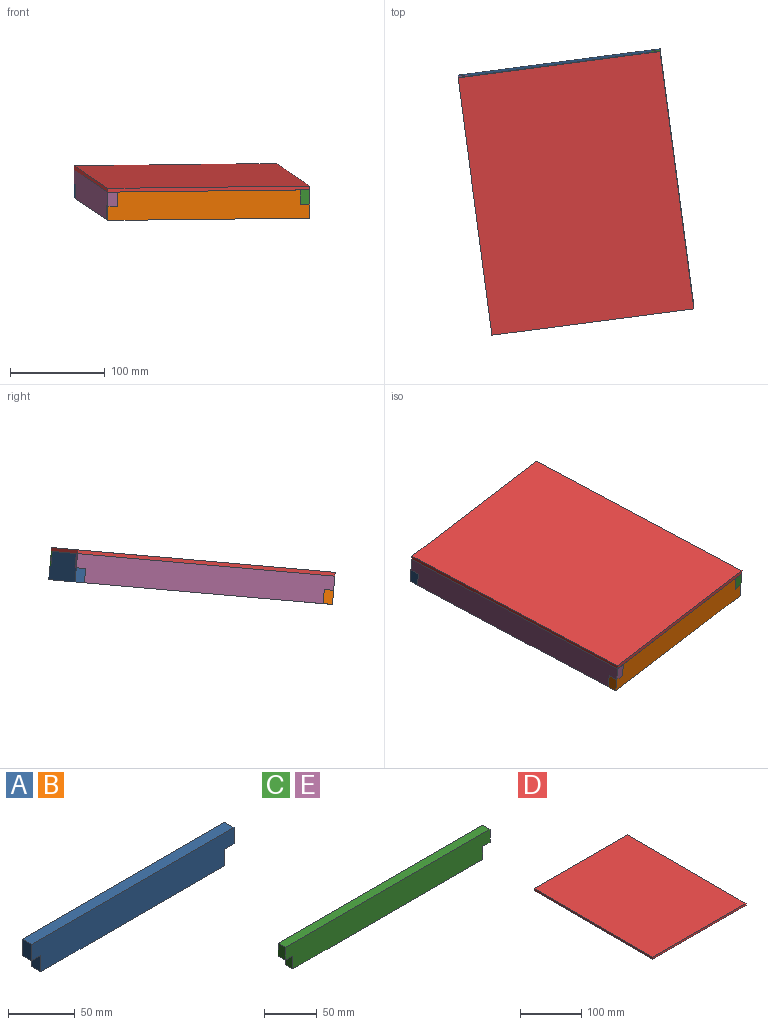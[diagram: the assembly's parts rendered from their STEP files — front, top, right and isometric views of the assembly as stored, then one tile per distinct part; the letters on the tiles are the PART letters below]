
ASSEMBLY  parts=5 mates=4
PART A: 10 faces, bbox 215x10x30 mm
  f0: plane 195x10mm, normal (0,0,-1), area 1950mm2, adj f1,f2,f7,f9
  f1: plane 215x30mm, normal (0,-1,0), area 6150mm2, adj f0,f3,f4,f5,f6,f7,f8,f9
  f2: plane 215x30mm, normal (0,1,0), area 6150mm2, adj f0,f3,f4,f5,f6,f7,f8,f9
  f3: plane 215x10mm, normal (0,0,1), area 2150mm2, adj f1,f2,f4,f5
  f4: plane 15x10mm, normal (-1,0,0), area 150mm2, adj f1,f2,f3,f6
  f5: plane 15x10mm, normal (1,0,0), area 150mm2, adj f1,f2,f3,f8
  f6: plane 10x10mm, normal (0,0,-1), area 100mm2, adj f1,f2,f4,f7
  f7: plane 15x10mm, normal (-1,0,0), area 150mm2, adj f0,f1,f2,f6
  f8: plane 10x10mm, normal (0,0,-1), area 100mm2, adj f1,f2,f5,f9
  f9: plane 15x10mm, normal (1,0,0), area 150mm2, adj f0,f1,f2,f8
PART B: same geometry as A
PART C: 10 faces, bbox 275x10x30 mm
  f0: plane 255x10mm, normal (0,0,-1), area 2550mm2, adj f1,f2,f7,f9
  f1: plane 275x30mm, normal (0,-1,0), area 7950mm2, adj f0,f3,f4,f5,f6,f7,f8,f9
  f2: plane 275x30mm, normal (0,1,0), area 7950mm2, adj f0,f3,f4,f5,f6,f7,f8,f9
  f3: plane 275x10mm, normal (0,0,1), area 2750mm2, adj f1,f2,f4,f5
  f4: plane 15x10mm, normal (-1,0,0), area 150mm2, adj f1,f2,f3,f8
  f5: plane 15x10mm, normal (1,0,0), area 150mm2, adj f1,f2,f3,f6
  f6: plane 10x10mm, normal (0,0,-1), area 100mm2, adj f1,f2,f5,f7
  f7: plane 15x10mm, normal (1,0,0), area 150mm2, adj f0,f1,f2,f6
  f8: plane 10x10mm, normal (0,0,-1), area 100mm2, adj f1,f2,f4,f9
  f9: plane 15x10mm, normal (-1,0,0), area 150mm2, adj f0,f1,f2,f8
PART D: 6 faces, bbox 215x275x4 mm
  f0: plane 215x4mm, normal (0,1,0), area 860mm2, adj f1,f3,f4,f5
  f1: plane 275x4mm, normal (-1,0,0), area 1100mm2, adj f0,f2,f4,f5
  f2: plane 215x4mm, normal (0,-1,0), area 860mm2, adj f1,f3,f4,f5
  f3: plane 275x4mm, normal (1,0,0), area 1100mm2, adj f0,f2,f4,f5
  f4: plane 275x215mm, normal (0,0,1), area 59125mm2, adj f0,f1,f2,f3
  f5: plane 275x215mm, normal (0,0,-1), area 59125mm2, adj f0,f1,f2,f3
PART E: same geometry as C
PLACE A rot(axis=(-0.06,1,0.04),179.7deg) t=(-256.14,264.74,100.44)mm fixed
PLACE B rot(axis=(-1,-0.06,0),175deg) t=(-251.52,-10.95,76.32)mm fixed
PLACE C rot(axis=(0.05,0.04,-1),82.7deg) t=(-153.16,187.47,75.33)mm fixed
PLACE D rot(axis=(-0.06,1,0.04),179.7deg) t=(-234,45.93,91.19)mm fixed
PLACE E rot(axis=(0.05,0.04,-1),82.7deg) t=(-356.43,160.99,73.01)mm fixed
MATE fastened D.f4 <-> A.f0  axis (0,0.09,-1) through (-271.66,262.21,106.1)mm
MATE fastened A.f1 <-> C.f9  axis (0.13,-0.99,-0.09) through (-163.77,268.83,76.56)mm
MATE fastened C.f7 <-> B.f1  axis (0.13,-0.99,-0.09) through (-130.7,16.95,54.53)mm
MATE fastened E.f9 <-> A.f1  axis (-0.13,0.99,0.09) through (-376.96,241.05,74.13)mm
